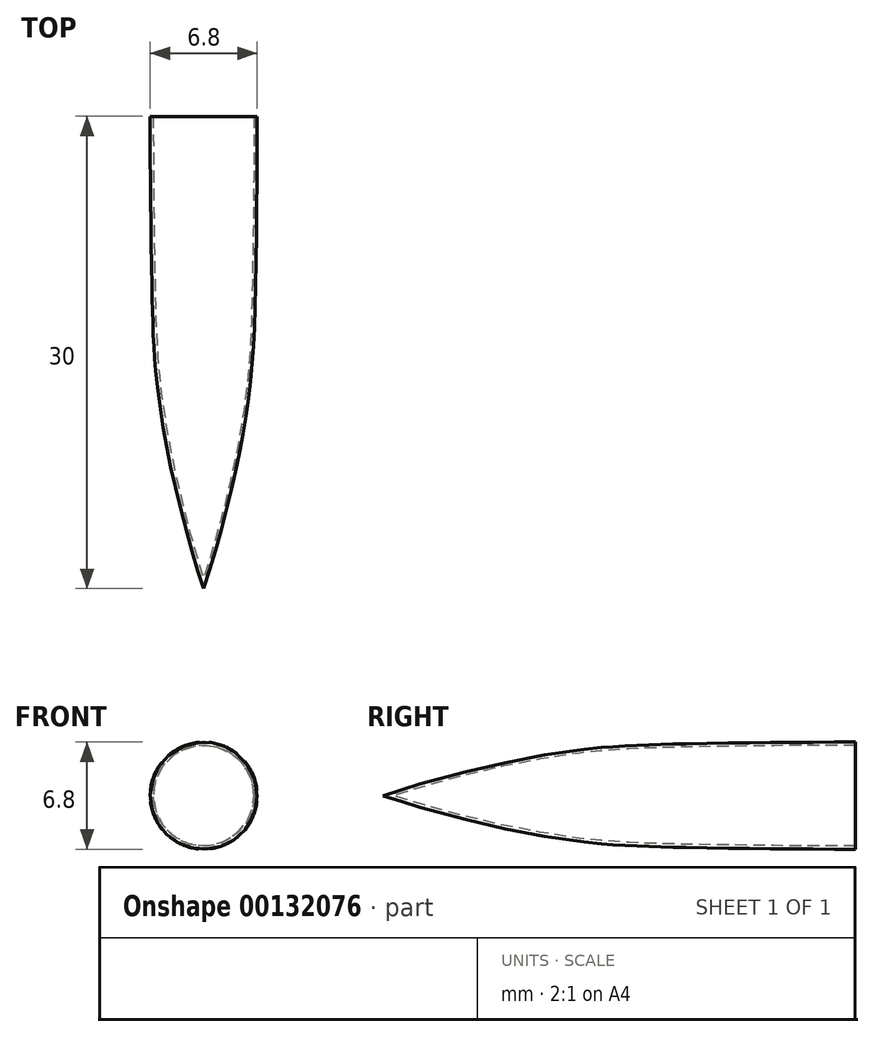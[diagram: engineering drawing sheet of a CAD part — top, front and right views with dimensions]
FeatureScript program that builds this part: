
annotation { "Feature Type Name" : "Feature", "Feature Type Description" : "" }
export const myFeature = defineFeature(function(context is Context, id is Id, definition is map)
    precondition{}
    {
        {
            var Q0;
            Q0=qCreatedBy(makeId("Top.planeOp"),FACE);
            var sketch = newSketch(context, id + "F0", { "sketchPlane" : qUnion([Q0])});
            skLineSegment(sketch, "E0", {"start": v(-42.57, 52.27) * mm, "end": v(-42.57, 22.27) * mm});
            skFitSpline(sketch, "E1", {"points": [v(-39.17, 52.27) * mm, v(-39.27, 41.88) * mm, v(-39.6, 35.3) * mm, v(-40.63, 29.28) * mm, v(-42.57, 22.27) * mm], "startDerivative": vector(0.07, -22.4) * mm, "endDerivative": vector(-8.86, -26.67) * mm});
            skLineSegment(sketch, "E2", {"start": v(-39.17, 52.27) * mm, "end": v(-42.57, 52.27) * mm});
            skSolve(sketch);
        }
        {
            var Q0;
            Q0 = qSketchRegion(id + "F0", true);
            var Q1;
            Q1=sQuery(id+"F0.wireOp",EDGE,"E0");
            revolve(context, id + "F1", {"entities" : qUnion([Q0]), "axis" : qUnion([Q1]), "revolveType" : RevolveType.FULL});
        }
        {
            var Q0;
            Q0=makeQuery(id+"F1.opRevolve","SWEPT_FACE",FACE,{"disambiguationData":[OSD([sQuery(id+"F0.wireOp",EDGE,"E2")])]});
            shell(context, id + "F2", {"entities" : qUnion([Q0]), "thickness" : 0.2 * mm});
        }
    });
